# Revit family: 1368xxx Cabin Wall (CE)
name_source: partatom
category: Lighting Fixtures
units: mm (PartAtom-declared; Revit-internal decimal feet)

## family parameters
Always vertical = Yes
Cut with Voids When Loaded = No
Host = Wall
Light Source = No
OmniClass Number = 23.80.70.00
OmniClass Title = Lighting
Part Type = Normal
Room Calculation Point = No
Round Connector Dimension = Use Diameter
Shared = No

## types (2) — shared parameters
Driver Required = No
Manufacturer = Astro Lighting Ltd
Manufacturer URL - Europe and Rest of World = www.astrolighting.com
Manufacturer URL - North America = us.astrolighting.com
URL = www.astrolighting.com
zero-valued in all types: Default Elevation

## per-type parameters (varying)
| type | ADA compliant | Dimmable | Dimming Method | Driver Included | Efficacy (lm/w) | Electrical Class | Lamp | Light Source Fixed | Location / IP Rating | Main Finish | Main Material | Power (Watts) | Product CCT | Product CRI | Product Dimensions (MM) | Product Location | Product Name | Product SKU | Product Weight (KG) |
| CE | N / A | Yes | Lamp Dependent | Not Applicable | Not Applicable | 1 | Incandescent | Yes | IP44 | Various | Metal - Zinc | Lamp Dependent | Lamp Dependent | Lamp Dependent | 220 x 116 x 183 | Outdoor | Cabin Wall | 1368003 | 1.54 |
| ETL |  |  |  |  |  | 0 |  |  | DAMP |  | Metal - Steel |  | 2700K / 3000K | 80 / 90 |  | Bathroom |  | 1234001 |  |

## geometry (parser evidence)
native form markers: Sweep x3
no freeform markers — native parametric forms only
